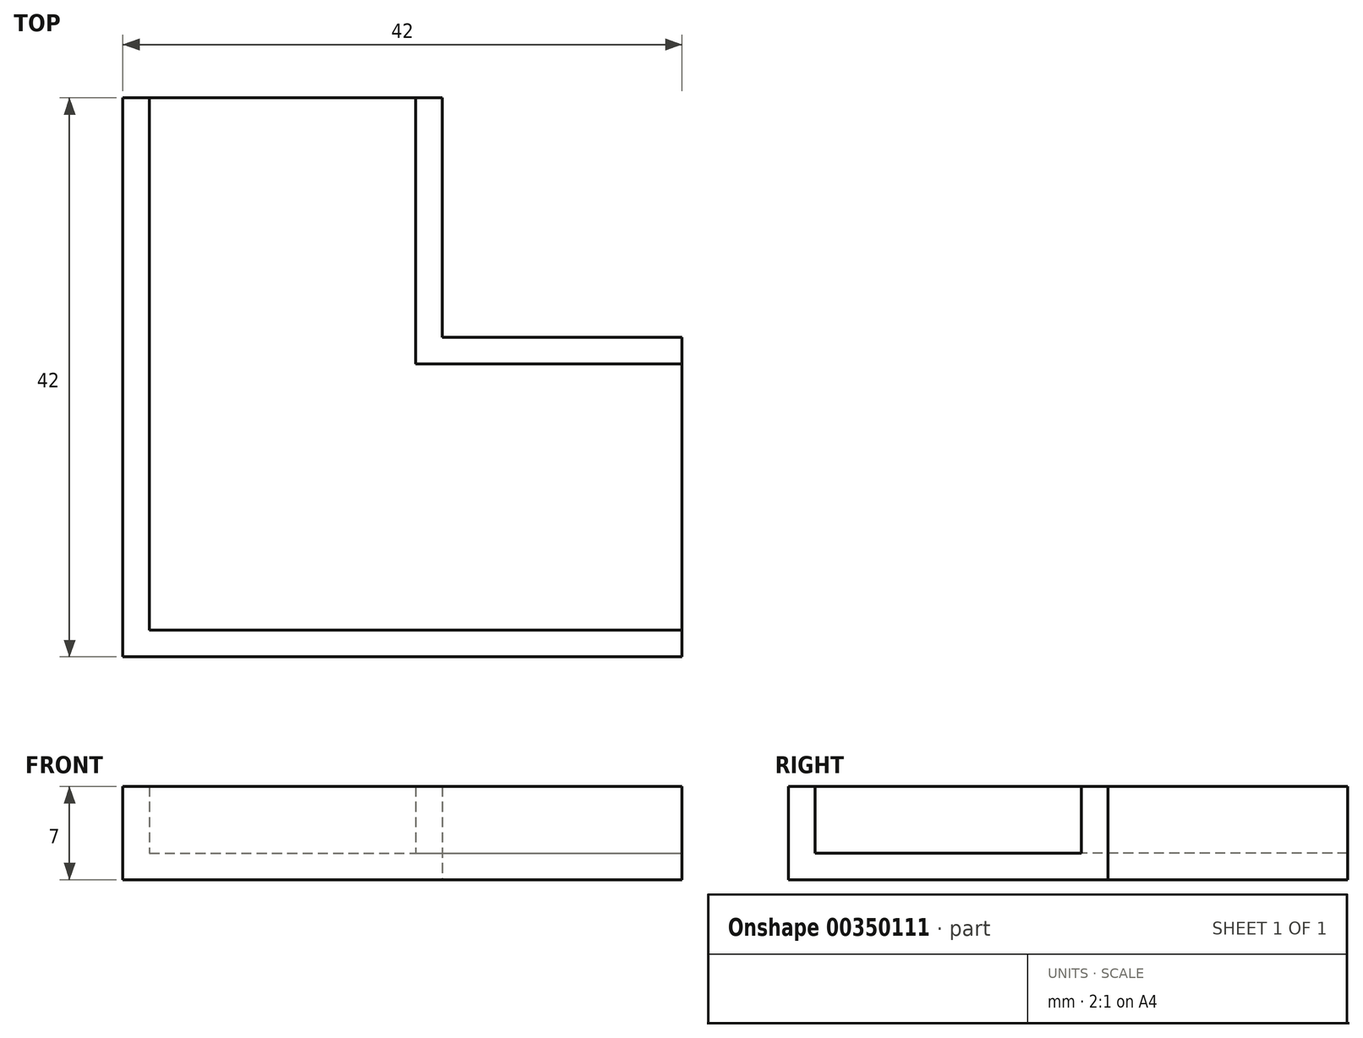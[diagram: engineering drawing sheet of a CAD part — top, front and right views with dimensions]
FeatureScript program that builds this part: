
annotation { "Feature Type Name" : "Feature", "Feature Type Description" : "" }
export const myFeature = defineFeature(function(context is Context, id is Id, definition is map)
    precondition{}
    {
        {
            var Q0;
            Q0=qCreatedBy(makeId("Top.planeOp"),FACE);
            var sketch = newSketch(context, id + "F0", { "sketchPlane" : qUnion([Q0])});
            skLineSegment(sketch, "E0.bottom", {"start": v(-20, 20) * mm, "end": v(0, 20) * mm});
            skLineSegment(sketch, "E0.top", {"start": v(-20, -20) * mm, "end": v(20, -20) * mm});
            skLineSegment(sketch, "E0.left", {"start": v(-20, 20) * mm, "end": v(-20, -20) * mm});
            skLineSegment(sketch, "E0.right", {"start": v(20, 0) * mm, "end": v(20, -20) * mm});
            skPoint(sketch, "E0.middle", {"position": v(0, 0) * mm});
            skLineSegment(sketch, "E1", {"start": v(0, 20) * mm, "end": v(0, 0) * mm});
            skLineSegment(sketch, "E2", {"start": v(0, 0) * mm, "end": v(20, 0) * mm});
            skPoint(sketch, "E3.orphan", {"position": v(20, 20) * mm});
            skSolve(sketch);
        }
        {
            var Q0;
            Q0=qSketchRegion(id+"F0",true);
            extrude(context, id + "F1", {"entities" : qUnion([Q0]), "depth" : 5 * mm});
        }
        {
            var Q0;
            Q0=makeQuery(id+"F1.opExtrude","CAP_FACE",FACE,{"disambiguationData":[OSD([sQuery(id+"F0.wireOp",EDGE,"E0.bottom"),sQuery(id+"F0.wireOp",EDGE,"E0.top"),sQuery(id+"F0.wireOp",EDGE,"E0.left"),sQuery(id+"F0.wireOp",EDGE,"E0.right"),sQuery(id+"F0.wireOp",EDGE,"E1"),sQuery(id+"F0.wireOp",EDGE,"E2")])],"isStart":false});
            var Q1;
            Q1=makeQuery(id+"F1.opExtrude","SWEPT_FACE",FACE,{"disambiguationData":[OSD([sQuery(id+"F0.wireOp",EDGE,"E0.right")])]});
            var Q2;
            Q2=makeQuery(id+"F1.opExtrude","SWEPT_FACE",FACE,{"disambiguationData":[OSD([sQuery(id+"F0.wireOp",EDGE,"E0.bottom")])]});
            shell(context, id + "F2", {"entities" : qUnion([Q0, Q1, Q2]), "thickness" : 2 * mm, "oppositeDirection" : true});
        }
    });
